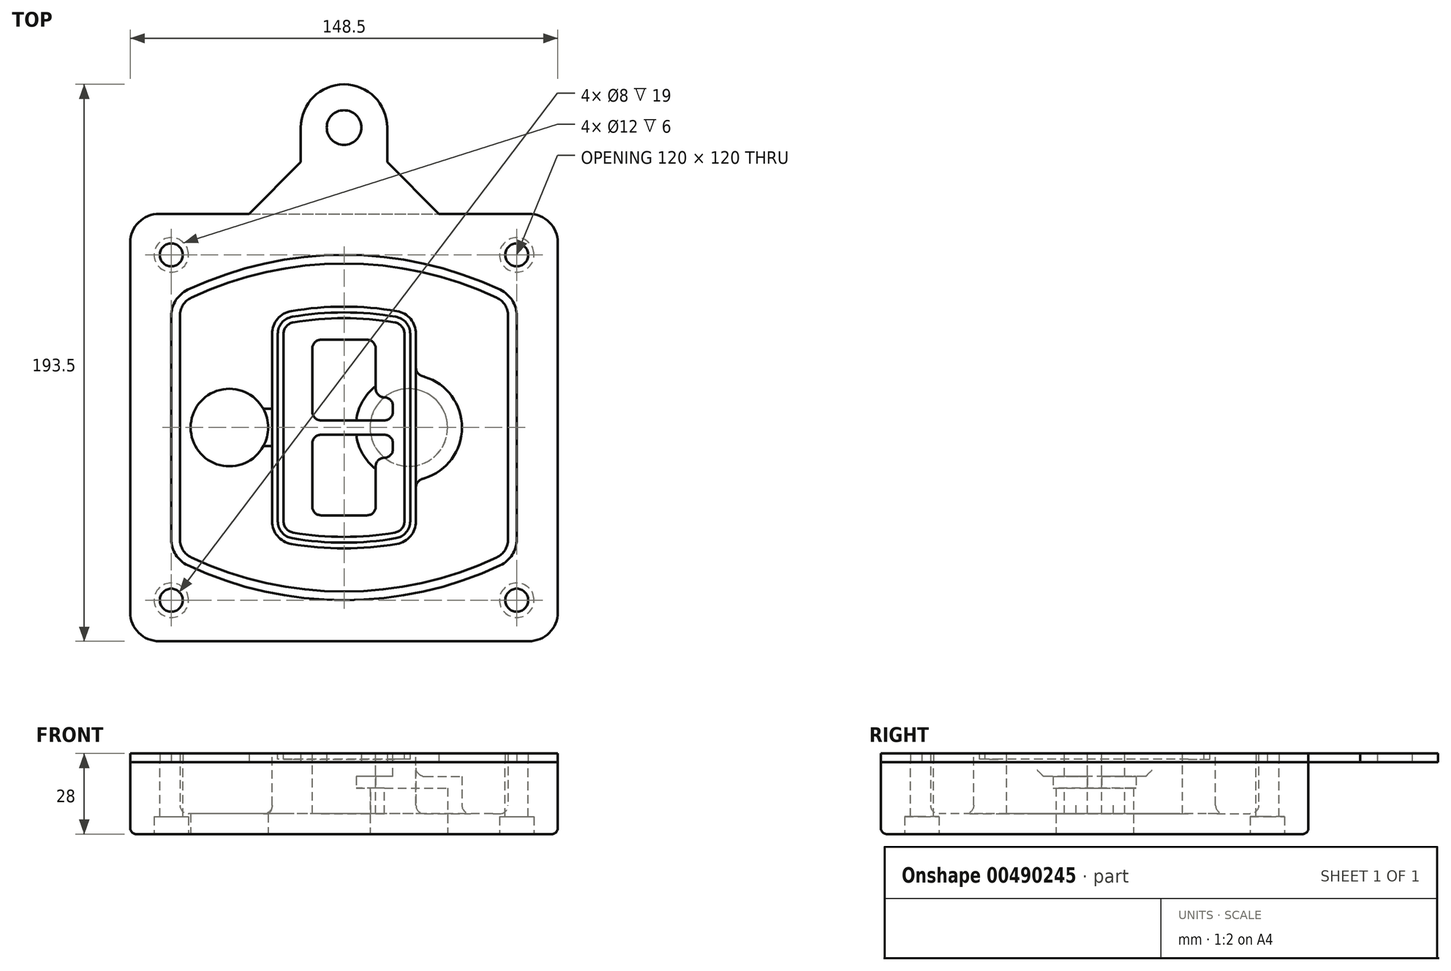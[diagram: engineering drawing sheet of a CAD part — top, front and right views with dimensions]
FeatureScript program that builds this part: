
annotation { "Feature Type Name" : "Feature", "Feature Type Description" : "" }
export const myFeature = defineFeature(function(context is Context, id is Id, definition is map)
    precondition{}
    {
        {
            var Q0;
            Q0=qCreatedBy(makeId("Top.planeOp"),FACE);
            var sketch = newSketch(context, id + "F0", { "sketchPlane" : qUnion([Q0])});
            skPoint(sketch, "E0.rect.middle", {"position": v(0, 0) * mm});
            skLineSegment(sketch, "E1.bottom", {"start": v(-64.25, -74.25) * mm, "end": v(64.25, -74.25) * mm});
            skLineSegment(sketch, "E1.top", {"start": v(-64.25, 74.25) * mm, "end": v(64.25, 74.25) * mm});
            skLineSegment(sketch, "E1.left", {"start": v(-74.25, -64.25) * mm, "end": v(-74.25, 64.25) * mm});
            skLineSegment(sketch, "E1.right", {"start": v(74.25, -64.25) * mm, "end": v(74.25, 64.25) * mm});
            skLineSegment(sketch, "E2", {"start": v(-74.25, 74.25) * mm, "end": v(74.25, -74.25) * mm, "construction": true});
            skLineSegment(sketch, "E3", {"start": v(74.25, 74.25) * mm, "end": v(-74.25, -74.25) * mm, "construction": true});
            skCircle(sketch, "E4", {"center": v(-60, 60) * mm, "radius": 4 * mm});
            skCircle(sketch, "E5", {"center": v(60, 60) * mm, "radius": 4 * mm});
            skCircle(sketch, "E6", {"center": v(60, -60) * mm, "radius": 4 * mm});
            skCircle(sketch, "E7", {"center": v(-60, -60) * mm, "radius": 4 * mm});
            skLineSegment(sketch, "E8", {"start": v(-60, 60) * mm, "end": v(60, 60) * mm, "construction": true});
            skLineSegment(sketch, "E9", {"start": v(60, 60) * mm, "end": v(60, -60) * mm, "construction": true});
            skLineSegment(sketch, "E10", {"start": v(60, -60) * mm, "end": v(-60, -60) * mm, "construction": true});
            skLineSegment(sketch, "E11", {"start": v(-60, -60) * mm, "end": v(-60, 60) * mm, "construction": true});
            skLineSegment(sketch, "E12", {"start": v(-60, 38.83) * mm, "end": v(-60, -38.83) * mm});
            skLineSegment(sketch, "E13", {"start": v(60, 38.83) * mm, "end": v(60, -38.83) * mm});
            skArc(sketch, "E14", {"start": v(54.26, 47.88) * mm, "mid": v(0, 60) * mm, "end": v(-54.26, 47.88) * mm});
            skArc(sketch, "E15", {"start": v(-54.26, -47.88) * mm, "mid": v(0, -60) * mm, "end": v(54.26, -47.88) * mm});
            skLineSegment(sketch, "E16", {"start": v(-60, 0) * mm, "end": v(60, 0) * mm, "construction": true});
            skPoint(sketch, "E17.visualSharp", {"position": v(-60, -45) * mm});
            skArc(sketch, "E17.filletArc", {"start": v(-60, -38.83) * mm, "mid": v(-58.44, -44.2) * mm, "end": v(-54.26, -47.88) * mm});
            skPoint(sketch, "E18.visualSharp", {"position": v(-60, 45) * mm});
            skArc(sketch, "E18.filletArc", {"start": v(-54.26, 47.88) * mm, "mid": v(-58.44, 44.2) * mm, "end": v(-60, 38.83) * mm});
            skPoint(sketch, "E19.visualSharp", {"position": v(60, 45) * mm});
            skArc(sketch, "E19.filletArc", {"start": v(60, 38.83) * mm, "mid": v(58.44, 44.2) * mm, "end": v(54.26, 47.88) * mm});
            skPoint(sketch, "E20.visualSharp", {"position": v(60, -45) * mm});
            skArc(sketch, "E20.filletArc", {"start": v(54.26, -47.88) * mm, "mid": v(58.44, -44.2) * mm, "end": v(60, -38.83) * mm});
            skPoint(sketch, "E21.visualSharp", {"position": v(-74.25, 74.25) * mm});
            skArc(sketch, "E21.filletArc", {"start": v(-64.25, 74.25) * mm, "mid": v(-71.32, 71.32) * mm, "end": v(-74.25, 64.25) * mm});
            skPoint(sketch, "E22.visualSharp", {"position": v(74.25, 74.25) * mm});
            skArc(sketch, "E22.filletArc", {"start": v(74.25, 64.25) * mm, "mid": v(71.32, 71.32) * mm, "end": v(64.25, 74.25) * mm});
            skPoint(sketch, "E23.visualSharp", {"position": v(74.25, -74.25) * mm});
            skArc(sketch, "E23.filletArc", {"start": v(64.25, -74.25) * mm, "mid": v(71.32, -71.32) * mm, "end": v(74.25, -64.25) * mm});
            skPoint(sketch, "E24.visualSharp", {"position": v(-74.25, -74.25) * mm});
            skArc(sketch, "E24.filletArc", {"start": v(-74.25, -64.25) * mm, "mid": v(-71.32, -71.32) * mm, "end": v(-64.25, -74.25) * mm});
            skArc(sketch, "E25.0", {"start": v(57, 38.83) * mm, "mid": v(55.9, 42.58) * mm, "end": v(52.98, 45.17) * mm});
            skLineSegment(sketch, "E25.1", {"start": v(57, 38.83) * mm, "end": v(57, -38.83) * mm});
            skArc(sketch, "E25.2", {"start": v(52.98, -45.17) * mm, "mid": v(55.9, -42.58) * mm, "end": v(57, -38.83) * mm});
            skArc(sketch, "E25.3", {"start": v(-52.98, -45.17) * mm, "mid": v(0, -57) * mm, "end": v(52.98, -45.17) * mm});
            skArc(sketch, "E25.4", {"start": v(-57, -38.83) * mm, "mid": v(-55.9, -42.58) * mm, "end": v(-52.98, -45.17) * mm});
            skArc(sketch, "E25.5", {"start": v(52.98, 45.17) * mm, "mid": v(0, 57) * mm, "end": v(-52.98, 45.17) * mm});
            skLineSegment(sketch, "E25.6", {"start": v(-57, 38.83) * mm, "end": v(-57, -38.83) * mm});
            skArc(sketch, "E25.7", {"start": v(-52.98, 45.17) * mm, "mid": v(-55.9, 42.58) * mm, "end": v(-57, 38.83) * mm});
            skArc(sketch, "E26.0", {"start": v(-55.96, 51.5) * mm, "mid": v(-61.82, 46.33) * mm, "end": v(-64, 38.83) * mm});
            skArc(sketch, "E26.1", {"start": v(55.96, 51.5) * mm, "mid": v(0, 64) * mm, "end": v(-55.96, 51.5) * mm});
            skArc(sketch, "E26.2", {"start": v(64, 38.83) * mm, "mid": v(61.82, 46.33) * mm, "end": v(55.96, 51.5) * mm});
            skLineSegment(sketch, "E26.3", {"start": v(64, 38.83) * mm, "end": v(64, -38.83) * mm});
            skArc(sketch, "E26.4", {"start": v(55.96, -51.5) * mm, "mid": v(61.82, -46.33) * mm, "end": v(64, -38.83) * mm});
            skLineSegment(sketch, "E26.5", {"start": v(-64, 38.83) * mm, "end": v(-64, -38.83) * mm});
            skArc(sketch, "E26.6", {"start": v(-55.96, -51.5) * mm, "mid": v(0, -64) * mm, "end": v(55.96, -51.5) * mm});
            skArc(sketch, "E26.7", {"start": v(-64, -38.83) * mm, "mid": v(-61.82, -46.33) * mm, "end": v(-55.96, -51.5) * mm});
            skSolve(sketch);
        }
        {
            var Q0;
            Q0=makeQuery(id+"F0.imprint","IMPRINT",FACE,{"disambiguationData":[TD([[makeQuery(id+"F0.imprint","IMPRINT",EDGE,{"derivedFrom":sQuery(id+"F0.wireOp",EDGE,"E1.bottom")}),1.0]])]});
            var Q1;
            Q1=makeQuery(id+"F0.imprint","IMPRINT",FACE,{"disambiguationData":[TD([[makeQuery(id+"F0.imprint","IMPRINT",EDGE,{"derivedFrom":sQuery(id+"F0.wireOp",EDGE,"E12")}),1.0]])]});
            var Q2;
            Q2=makeQuery(id+"F0.imprint","IMPRINT",FACE,{"disambiguationData":[TD([[makeQuery(id+"F0.imprint","IMPRINT",EDGE,{"derivedFrom":sQuery(id+"F0.wireOp",EDGE,"E25.0")}),1.0]])]});
            var Q3;
            Q3=makeQuery(id+"F0.imprint","IMPRINT",FACE,{"disambiguationData":[TD([[makeQuery(id+"F0.imprint","IMPRINT",EDGE,{"derivedFrom":sQuery(id+"F0.wireOp",EDGE,"E12")}),-1.0]])]});
            extrude(context, id + "F1", {"entities" : qUnion([Q0, Q1, Q2, Q3]), "oppositeDirection" : true, "depth" : 25 * mm});
        }
        {
            var Q0;
            Q0=makeQuery(id+"F0.imprint","IMPRINT",FACE,{"disambiguationData":[TD([[makeQuery(id+"F0.imprint","IMPRINT",EDGE,{"derivedFrom":sQuery(id+"F0.wireOp",EDGE,"E12")}),1.0]])]});
            extrude(context, id + "F2", {"entities" : qUnion([Q0]), "operationType" : NewBodyOperationType.ADD, "depth" : 3 * mm});
        }
        {
            var Q0;
            Q0=makeQuery(id+"F0.imprint","IMPRINT",FACE,{"disambiguationData":[TD([[makeQuery(id+"F0.imprint","IMPRINT",EDGE,{"derivedFrom":sQuery(id+"F0.wireOp",EDGE,"E25.0")}),1.0]])]});
            extrude(context, id + "F3", {"entities" : qUnion([Q0]), "operationType" : NewBodyOperationType.REMOVE, "oppositeDirection" : true, "depth" : 18 * mm});
        }
        {
            var Q0;
            Q0=makeQuery(id+"F2.opExtrude","CAP_FACE",FACE,{"disambiguationData":[OSD([sQuery(id+"F0.wireOp",EDGE,"E12"),sQuery(id+"F0.wireOp",EDGE,"E13"),sQuery(id+"F0.wireOp",EDGE,"E14"),sQuery(id+"F0.wireOp",EDGE,"E15"),sQuery(id+"F0.wireOp",EDGE,"E17.filletArc"),sQuery(id+"F0.wireOp",EDGE,"E18.filletArc"),sQuery(id+"F0.wireOp",EDGE,"E19.filletArc"),sQuery(id+"F0.wireOp",EDGE,"E20.filletArc"),sQuery(id+"F0.wireOp",EDGE,"E25.0"),sQuery(id+"F0.wireOp",EDGE,"E25.1"),sQuery(id+"F0.wireOp",EDGE,"E25.2"),sQuery(id+"F0.wireOp",EDGE,"E25.3"),sQuery(id+"F0.wireOp",EDGE,"E25.4"),sQuery(id+"F0.wireOp",EDGE,"E25.5"),sQuery(id+"F0.wireOp",EDGE,"E25.6"),sQuery(id+"F0.wireOp",EDGE,"E25.7")])],"isStart":false});
            var sketch = newSketch(context, id + "F4", { "sketchPlane" : qUnion([Q0])});
            skArc(sketch, "E27.0", {"start": v(-18.34, -40.45) * mm, "mid": v(0, -42) * mm, "end": v(18.34, -40.45) * mm});
            skArc(sketch, "E28.0", {"start": v(18.34, 40.45) * mm, "mid": v(0, 42) * mm, "end": v(-18.34, 40.45) * mm});
            skLineSegment(sketch, "E29", {"start": v(-25, 32.57) * mm, "end": v(-25, -32.57) * mm});
            skLineSegment(sketch, "E30", {"start": v(25, 32.57) * mm, "end": v(25, -32.57) * mm});
            skLineSegment(sketch, "E31", {"start": v(-25, 39.1) * mm, "end": v(25, 39.1) * mm, "construction": true});
            skLineSegment(sketch, "E32", {"start": v(-25, -39.1) * mm, "end": v(25, -39.1) * mm, "construction": true});
            skPoint(sketch, "E33.visualSharp", {"position": v(-25, 39.1) * mm});
            skArc(sketch, "E33.filletArc", {"start": v(-18.34, 40.45) * mm, "mid": v(-23.11, 37.73) * mm, "end": v(-25, 32.57) * mm});
            skPoint(sketch, "E34.visualSharp", {"position": v(25, 39.1) * mm});
            skArc(sketch, "E34.filletArc", {"start": v(25, 32.57) * mm, "mid": v(23.11, 37.73) * mm, "end": v(18.34, 40.45) * mm});
            skPoint(sketch, "E35.visualSharp", {"position": v(25, -39.1) * mm});
            skArc(sketch, "E35.filletArc", {"start": v(18.34, -40.45) * mm, "mid": v(23.11, -37.73) * mm, "end": v(25, -32.57) * mm});
            skPoint(sketch, "E36.visualSharp", {"position": v(-25, -39.1) * mm});
            skArc(sketch, "E36.filletArc", {"start": v(-25, -32.57) * mm, "mid": v(-23.11, -37.73) * mm, "end": v(-18.34, -40.45) * mm});
            skArc(sketch, "E37.0", {"start": v(52.98, 45.17) * mm, "mid": v(0, 57) * mm, "end": v(-52.98, 45.17) * mm});
            skArc(sketch, "E37.1", {"start": v(-52.98, 45.17) * mm, "mid": v(-55.9, 42.58) * mm, "end": v(-57, 38.83) * mm});
            skLineSegment(sketch, "E37.2", {"start": v(-57, 38.83) * mm, "end": v(-57, -38.83) * mm});
            skArc(sketch, "E37.3", {"start": v(-57, -38.83) * mm, "mid": v(-55.9, -42.58) * mm, "end": v(-52.98, -45.17) * mm});
            skArc(sketch, "E37.4", {"start": v(-52.98, -45.17) * mm, "mid": v(0, -57) * mm, "end": v(52.98, -45.17) * mm});
            skArc(sketch, "E37.5", {"start": v(52.98, -45.17) * mm, "mid": v(55.9, -42.58) * mm, "end": v(57, -38.83) * mm});
            skLineSegment(sketch, "E37.6", {"start": v(57, 38.83) * mm, "end": v(57, -38.83) * mm});
            skArc(sketch, "E37.7", {"start": v(57, 38.83) * mm, "mid": v(55.9, 42.58) * mm, "end": v(52.98, 45.17) * mm});
            skLineSegment(sketch, "E38.0", {"start": v(23, 32.57) * mm, "end": v(23, -32.57) * mm});
            skArc(sketch, "E38.1", {"start": v(18, -38.48) * mm, "mid": v(21.58, -36.44) * mm, "end": v(23, -32.57) * mm});
            skArc(sketch, "E38.2", {"start": v(-18, -38.48) * mm, "mid": v(0, -40) * mm, "end": v(18, -38.48) * mm});
            skArc(sketch, "E38.3", {"start": v(-23, -32.57) * mm, "mid": v(-21.58, -36.44) * mm, "end": v(-18, -38.48) * mm});
            skLineSegment(sketch, "E38.4", {"start": v(-23, 32.57) * mm, "end": v(-23, -32.57) * mm});
            skArc(sketch, "E38.5", {"start": v(23, 32.57) * mm, "mid": v(21.58, 36.44) * mm, "end": v(18, 38.48) * mm});
            skArc(sketch, "E38.6", {"start": v(-18, 38.48) * mm, "mid": v(-21.58, 36.44) * mm, "end": v(-23, 32.57) * mm});
            skArc(sketch, "E38.7", {"start": v(18, 38.48) * mm, "mid": v(0, 40) * mm, "end": v(-18, 38.48) * mm});
            skArc(sketch, "E39.0", {"start": v(21, 32.57) * mm, "mid": v(20.06, 35.15) * mm, "end": v(17.67, 36.5) * mm});
            skLineSegment(sketch, "E39.1", {"start": v(21, 32.57) * mm, "end": v(21, -32.57) * mm});
            skArc(sketch, "E39.2", {"start": v(17.67, -36.5) * mm, "mid": v(20.06, -35.15) * mm, "end": v(21, -32.57) * mm});
            skArc(sketch, "E39.3", {"start": v(-17.67, -36.5) * mm, "mid": v(0, -38) * mm, "end": v(17.67, -36.5) * mm});
            skArc(sketch, "E39.4", {"start": v(-21, -32.57) * mm, "mid": v(-20.06, -35.15) * mm, "end": v(-17.67, -36.5) * mm});
            skArc(sketch, "E39.5", {"start": v(17.67, 36.5) * mm, "mid": v(0, 38) * mm, "end": v(-17.67, 36.5) * mm});
            skLineSegment(sketch, "E39.6", {"start": v(-21, 32.57) * mm, "end": v(-21, -32.57) * mm});
            skArc(sketch, "E39.7", {"start": v(-17.67, 36.5) * mm, "mid": v(-20.06, 35.15) * mm, "end": v(-21, 32.57) * mm});
            skLineSegment(sketch, "E40", {"start": v(-25, 0) * mm, "end": v(25, 0) * mm, "construction": true});
            skLineSegment(sketch, "E41", {"start": v(-11, 5.5) * mm, "end": v(-11, 27.5) * mm});
            skLineSegment(sketch, "E42", {"start": v(-8, 30.5) * mm, "end": v(8, 30.5) * mm});
            skLineSegment(sketch, "E43", {"start": v(11, 27.5) * mm, "end": v(11, 13.5) * mm});
            skLineSegment(sketch, "E44", {"start": v(14, 10.5) * mm, "end": v(14, 10.5) * mm});
            skLineSegment(sketch, "E45", {"start": v(17, 7.5) * mm, "end": v(17, 5.5) * mm});
            skLineSegment(sketch, "E46", {"start": v(14, 2.5) * mm, "end": v(-8, 2.5) * mm});
            skPoint(sketch, "E47.visualSharp", {"position": v(-11, 30.5) * mm});
            skArc(sketch, "E47.filletArc", {"start": v(-8, 30.5) * mm, "mid": v(-10.12, 29.62) * mm, "end": v(-11, 27.5) * mm});
            skPoint(sketch, "E48.visualSharp", {"position": v(11, 30.5) * mm});
            skArc(sketch, "E48.filletArc", {"start": v(11, 27.5) * mm, "mid": v(10.12, 29.62) * mm, "end": v(8, 30.5) * mm});
            skPoint(sketch, "E49.visualSharp", {"position": v(11, 10.5) * mm});
            skArc(sketch, "E49.filletArc", {"start": v(11, 13.5) * mm, "mid": v(11.88, 11.38) * mm, "end": v(14, 10.5) * mm});
            skPoint(sketch, "E50.visualSharp", {"position": v(17, 10.5) * mm});
            skArc(sketch, "E50.filletArc", {"start": v(17, 7.5) * mm, "mid": v(16.12, 9.62) * mm, "end": v(14, 10.5) * mm});
            skPoint(sketch, "E51.visualSharp", {"position": v(17, 2.5) * mm});
            skArc(sketch, "E51.filletArc", {"start": v(14, 2.5) * mm, "mid": v(16.12, 3.38) * mm, "end": v(17, 5.5) * mm});
            skPoint(sketch, "E52.visualSharp", {"position": v(-11, 2.5) * mm});
            skArc(sketch, "E52.filletArc", {"start": v(-11, 5.5) * mm, "mid": v(-10.12, 3.38) * mm, "end": v(-8, 2.5) * mm});
            skLineSegment(sketch, "E53.0.MirrorCS", {"start": v(14, -2.5) * mm, "end": v(-8, -2.5) * mm});
            skArc(sketch, "E54.0.MirrorCS", {"start": v(-11, -5.5) * mm, "mid": v(-10.12, -3.38) * mm, "end": v(-8, -2.5) * mm});
            skLineSegment(sketch, "E55.0.MirrorCS", {"start": v(-11, -5.5) * mm, "end": v(-11, -27.5) * mm});
            skArc(sketch, "E56.0.MirrorCS", {"start": v(-8, -30.5) * mm, "mid": v(-10.12, -29.62) * mm, "end": v(-11, -27.5) * mm});
            skLineSegment(sketch, "E57.0.MirrorCS", {"start": v(-8, -30.5) * mm, "end": v(8, -30.5) * mm});
            skArc(sketch, "E58.0.MirrorCS", {"start": v(11, -27.5) * mm, "mid": v(10.12, -29.62) * mm, "end": v(8, -30.5) * mm});
            skLineSegment(sketch, "E59.0.MirrorCS", {"start": v(11, -27.5) * mm, "end": v(11, -13.5) * mm});
            skArc(sketch, "E60.0.MirrorCS", {"start": v(11, -13.5) * mm, "mid": v(11.88, -11.38) * mm, "end": v(14, -10.5) * mm});
            skArc(sketch, "E61.0.MirrorCS", {"start": v(17, -7.5) * mm, "mid": v(16.12, -9.62) * mm, "end": v(14, -10.5) * mm});
            skLineSegment(sketch, "E62.0.MirrorCS", {"start": v(17, -7.5) * mm, "end": v(17, -5.5) * mm});
            skArc(sketch, "E63.0.MirrorCS", {"start": v(14, -2.5) * mm, "mid": v(16.12, -3.38) * mm, "end": v(17, -5.5) * mm});
            skSolve(sketch);
        }
        {
            var Q0;
            Q0=makeQuery(id+"F4.imprint","IMPRINT",FACE,{"disambiguationData":[TD([[makeQuery(id+"F4.imprint","IMPRINT",EDGE,{"derivedFrom":sQuery(id+"F4.wireOp",EDGE,"E27.0")}),1.0]])]});
            var Q1;
            Q1=makeQuery(id+"F4.imprint","IMPRINT",FACE,{"disambiguationData":[TD([[makeQuery(id+"F4.imprint","IMPRINT",EDGE,{"derivedFrom":sQuery(id+"F4.wireOp",EDGE,"E38.0")}),-1.0]])]});
            var Q2;
            Q2=makeQuery(id+"F4.imprint","IMPRINT",FACE,{"disambiguationData":[TD([[makeQuery(id+"F4.imprint","IMPRINT",EDGE,{"derivedFrom":sQuery(id+"F4.wireOp",EDGE,"E39.0")}),1.0]])]});
            extrude(context, id + "F5", {"entities" : qUnion([Q0, Q1, Q2]), "operationType" : NewBodyOperationType.ADD, "endBound" : BoundingType.UP_TO_NEXT, "oppositeDirection" : true, "depth" : 25 * mm});
        }
        {
            var Q0;
            Q0=makeQuery(id+"F4.imprint","IMPRINT",FACE,{"disambiguationData":[TD([[makeQuery(id+"F4.imprint","IMPRINT",EDGE,{"derivedFrom":sQuery(id+"F4.wireOp",EDGE,"E38.0")}),-1.0]])]});
            extrude(context, id + "F6", {"entities" : qUnion([Q0]), "operationType" : NewBodyOperationType.REMOVE, "oppositeDirection" : true, "depth" : 2 * mm});
        }
        {
            var Q0;
            Q0=makeQuery(id+"F1.opExtrude","CAP_FACE",FACE,{"disambiguationData":[OSD([sQuery(id+"F0.wireOp",EDGE,"E1.bottom"),sQuery(id+"F0.wireOp",EDGE,"E1.top"),sQuery(id+"F0.wireOp",EDGE,"E1.left"),sQuery(id+"F0.wireOp",EDGE,"E1.right"),sQuery(id+"F0.wireOp",EDGE,"E4"),sQuery(id+"F0.wireOp",EDGE,"E5"),sQuery(id+"F0.wireOp",EDGE,"E6"),sQuery(id+"F0.wireOp",EDGE,"E7"),sQuery(id+"F0.wireOp",EDGE,"E21.filletArc"),sQuery(id+"F0.wireOp",EDGE,"E22.filletArc"),sQuery(id+"F0.wireOp",EDGE,"E23.filletArc"),sQuery(id+"F0.wireOp",EDGE,"E24.filletArc")])],"isStart":false});
            var sketch = newSketch(context, id + "F7", { "sketchPlane" : qUnion([Q0])});
            skCircle(sketch, "E64", {"center": v(22.5, 0) * mm, "radius": 13.47 * mm});
            skCircle(sketch, "E65", {"center": v(-39.81, 0) * mm, "radius": 13.47 * mm});
            skLineSegment(sketch, "E66", {"start": v(74.25, 0) * mm, "end": v(-74.25, 0) * mm});
            skCircle(sketch, "E67", {"center": v(22.5, 0) * mm, "radius": 18.47 * mm});
            skCircle(sketch, "E68", {"center": v(60, -60) * mm, "radius": 6 * mm});
            skCircle(sketch, "E69", {"center": v(-60, -60) * mm, "radius": 6 * mm});
            skCircle(sketch, "E70", {"center": v(-60, 60) * mm, "radius": 6 * mm});
            skCircle(sketch, "E71", {"center": v(60, 60) * mm, "radius": 6 * mm});
            skSolve(sketch);
        }
        {
            var Q0;
            {var subQ1=sQuery(id+"F7.wireOp",EDGE,"E66");var subQ4=sQuery(id+"F7.wireOp",EDGE,"E64");var subQ6=makeQuery(id+"F7.imprint","INTERSECT",VERTEX,{"disambiguationData":[OD(0.0)],"derivedFrom":[subQ4,subQ1]});Q0=makeQuery(id+"F7.imprint","IMPRINT",FACE,{"disambiguationData":[TD([[makeQuery(id+"F7.imprint","IMPRINT",EDGE,{"disambiguationData":[TD([[subQ6,-1.0]])],"derivedFrom":subQ4}),-1.0]])]});}
            var Q1;
            {var subQ0=sQuery(id+"F7.wireOp",EDGE,"E66");var subQ1=sQuery(id+"F7.wireOp",EDGE,"E64");var subQ3=makeQuery(id+"F7.imprint","INTERSECT",VERTEX,{"disambiguationData":[OD(0.0)],"derivedFrom":[subQ1,subQ0]});Q1=makeQuery(id+"F7.imprint","IMPRINT",FACE,{"disambiguationData":[TD([[makeQuery(id+"F7.imprint","IMPRINT",EDGE,{"disambiguationData":[TD([[subQ3,-1.0]])],"derivedFrom":subQ1}),1.0]])]});}
            var Q2;
            {var subQ0=sQuery(id+"F7.wireOp",EDGE,"E66");var subQ1=sQuery(id+"F7.wireOp",EDGE,"E64");var subQ3=makeQuery(id+"F7.imprint","INTERSECT",VERTEX,{"disambiguationData":[OD(0.0)],"derivedFrom":[subQ1,subQ0]});Q2=makeQuery(id+"F7.imprint","IMPRINT",FACE,{"disambiguationData":[TD([[makeQuery(id+"F7.imprint","IMPRINT",EDGE,{"disambiguationData":[TD([[subQ3,1.0]])],"derivedFrom":subQ1}),1.0]])]});}
            var Q3;
            {var subQ1=sQuery(id+"F7.wireOp",EDGE,"E66");var subQ4=sQuery(id+"F7.wireOp",EDGE,"E64");var subQ6=makeQuery(id+"F7.imprint","INTERSECT",VERTEX,{"disambiguationData":[OD(0.0)],"derivedFrom":[subQ4,subQ1]});Q3=makeQuery(id+"F7.imprint","IMPRINT",FACE,{"disambiguationData":[TD([[makeQuery(id+"F7.imprint","IMPRINT",EDGE,{"disambiguationData":[TD([[subQ6,1.0]])],"derivedFrom":subQ4}),-1.0]])]});}
            extrude(context, id + "F8", {"entities" : qUnion([Q0, Q1, Q2, Q3]), "operationType" : NewBodyOperationType.ADD, "oppositeDirection" : true, "depth" : 20 * mm});
        }
        {
            var Q0;
            {var subQ0=sQuery(id+"F7.wireOp",EDGE,"E66");var subQ1=sQuery(id+"F7.wireOp",EDGE,"E64");var subQ3=makeQuery(id+"F7.imprint","INTERSECT",VERTEX,{"disambiguationData":[OD(0.0)],"derivedFrom":[subQ1,subQ0]});Q0=makeQuery(id+"F7.imprint","IMPRINT",FACE,{"disambiguationData":[TD([[makeQuery(id+"F7.imprint","IMPRINT",EDGE,{"disambiguationData":[TD([[subQ3,-1.0]])],"derivedFrom":subQ1}),1.0]])]});}
            var Q1;
            {var subQ0=sQuery(id+"F7.wireOp",EDGE,"E66");var subQ1=sQuery(id+"F7.wireOp",EDGE,"E64");var subQ3=makeQuery(id+"F7.imprint","INTERSECT",VERTEX,{"disambiguationData":[OD(0.0)],"derivedFrom":[subQ1,subQ0]});Q1=makeQuery(id+"F7.imprint","IMPRINT",FACE,{"disambiguationData":[TD([[makeQuery(id+"F7.imprint","IMPRINT",EDGE,{"disambiguationData":[TD([[subQ3,1.0]])],"derivedFrom":subQ1}),1.0]])]});}
            extrude(context, id + "F9", {"entities" : qUnion([Q0, Q1]), "operationType" : NewBodyOperationType.REMOVE, "oppositeDirection" : true, "depth" : 16 * mm});
        }
        {
            var Q0;
            {var subQ0=sQuery(id+"F7.wireOp",EDGE,"E66");var subQ1=sQuery(id+"F7.wireOp",EDGE,"E65");var subQ3=makeQuery(id+"F7.imprint","INTERSECT",VERTEX,{"disambiguationData":[OD(0.0)],"derivedFrom":[subQ1,subQ0]});Q0=makeQuery(id+"F7.imprint","IMPRINT",FACE,{"disambiguationData":[TD([[makeQuery(id+"F7.imprint","IMPRINT",EDGE,{"disambiguationData":[TD([[subQ3,-1.0]])],"derivedFrom":subQ1}),1.0]])]});}
            var Q1;
            {var subQ0=sQuery(id+"F7.wireOp",EDGE,"E66");var subQ1=sQuery(id+"F7.wireOp",EDGE,"E65");var subQ3=makeQuery(id+"F7.imprint","INTERSECT",VERTEX,{"disambiguationData":[OD(0.0)],"derivedFrom":[subQ1,subQ0]});Q1=makeQuery(id+"F7.imprint","IMPRINT",FACE,{"disambiguationData":[TD([[makeQuery(id+"F7.imprint","IMPRINT",EDGE,{"disambiguationData":[TD([[subQ3,1.0]])],"derivedFrom":subQ1}),1.0]])]});}
            extrude(context, id + "F10", {"entities" : qUnion([Q0, Q1]), "operationType" : NewBodyOperationType.REMOVE, "oppositeDirection" : true, "depth" : 25 * mm});
        }
        {
            var Q0;
            Q0=makeQuery(id+"F7.imprint","IMPRINT",FACE,{"disambiguationData":[TD([[makeQuery(id+"F7.imprint","IMPRINT",EDGE,{"derivedFrom":sQuery(id+"F7.wireOp",EDGE,"E68")}),1.0]])]});
            var Q1;
            Q1=makeQuery(id+"F7.imprint","IMPRINT",FACE,{"disambiguationData":[TD([[makeQuery(id+"F7.imprint","IMPRINT",EDGE,{"derivedFrom":makeQuery(id+"F1.opExtrude","CAP_EDGE",EDGE,{"disambiguationData":[OSD([sQuery(id+"F0.wireOp",EDGE,"E5")])],"isStart":false})}),-1.0]])]});
            var Q2;
            Q2=makeQuery(id+"F7.imprint","IMPRINT",FACE,{"disambiguationData":[TD([[makeQuery(id+"F7.imprint","IMPRINT",EDGE,{"derivedFrom":sQuery(id+"F7.wireOp",EDGE,"E69")}),1.0]])]});
            var Q3;
            Q3=makeQuery(id+"F7.imprint","IMPRINT",FACE,{"disambiguationData":[TD([[makeQuery(id+"F7.imprint","IMPRINT",EDGE,{"derivedFrom":makeQuery(id+"F1.opExtrude","CAP_EDGE",EDGE,{"disambiguationData":[OSD([sQuery(id+"F0.wireOp",EDGE,"E4")])],"isStart":false})}),-1.0]])]});
            var Q4;
            Q4=makeQuery(id+"F7.imprint","IMPRINT",FACE,{"disambiguationData":[TD([[makeQuery(id+"F7.imprint","IMPRINT",EDGE,{"derivedFrom":sQuery(id+"F7.wireOp",EDGE,"E70")}),1.0]])]});
            var Q5;
            Q5=makeQuery(id+"F7.imprint","IMPRINT",FACE,{"disambiguationData":[TD([[makeQuery(id+"F7.imprint","IMPRINT",EDGE,{"derivedFrom":makeQuery(id+"F1.opExtrude","CAP_EDGE",EDGE,{"disambiguationData":[OSD([sQuery(id+"F0.wireOp",EDGE,"E7")])],"isStart":false})}),-1.0]])]});
            var Q6;
            Q6=makeQuery(id+"F7.imprint","IMPRINT",FACE,{"disambiguationData":[TD([[makeQuery(id+"F7.imprint","IMPRINT",EDGE,{"derivedFrom":sQuery(id+"F7.wireOp",EDGE,"E71")}),1.0]])]});
            var Q7;
            Q7=makeQuery(id+"F7.imprint","IMPRINT",FACE,{"disambiguationData":[TD([[makeQuery(id+"F7.imprint","IMPRINT",EDGE,{"derivedFrom":makeQuery(id+"F1.opExtrude","CAP_EDGE",EDGE,{"disambiguationData":[OSD([sQuery(id+"F0.wireOp",EDGE,"E6")])],"isStart":false})}),-1.0]])]});
            extrude(context, id + "F11", {"entities" : qUnion([Q0, Q1, Q2, Q3, Q4, Q5, Q6, Q7]), "operationType" : NewBodyOperationType.REMOVE, "oppositeDirection" : true, "depth" : 6 * mm});
        }
        {
            var Q0;
            Q0=makeQuery(id+"F9.boolean.opBoolean","COPY",FACE,{"derivedFrom":makeQuery(id+"F9.opExtrude","CAP_FACE",FACE,{"disambiguationData":[OSD([sQuery(id+"F7.wireOp",EDGE,"E64")])],"isStart":false})});
            var sketch = newSketch(context, id + "F12", { "sketchPlane" : qUnion([Q0])});
            skArc(sketch, "E72.0", {"start": v(11, 14.45) * mm, "mid": v(6.45, 9.13) * mm, "end": v(4.2, 2.5) * mm});
            skArc(sketch, "E72.1", {"start": v(4.2, -2.5) * mm, "mid": v(6.45, -9.13) * mm, "end": v(11, -14.45) * mm});
            skLineSegment(sketch, "E73", {"start": v(4.2, -2.5) * mm, "end": v(14, -2.5) * mm});
            skLineSegment(sketch, "E74.0", {"start": v(14, 2.5) * mm, "end": v(4.2, 2.5) * mm});
            skArc(sketch, "E74.1", {"start": v(14, 2.5) * mm, "mid": v(16.12, 3.38) * mm, "end": v(17, 5.5) * mm});
            skLineSegment(sketch, "E74.2", {"start": v(17, 7.5) * mm, "end": v(17, 5.5) * mm});
            skArc(sketch, "E74.3", {"start": v(17, 7.5) * mm, "mid": v(16.12, 9.62) * mm, "end": v(14, 10.5) * mm});
            skArc(sketch, "E74.4", {"start": v(11, 13.5) * mm, "mid": v(11.88, 11.38) * mm, "end": v(14, 10.5) * mm});
            skLineSegment(sketch, "E74.5", {"start": v(11, 14.45) * mm, "end": v(11, 13.5) * mm});
            skLineSegment(sketch, "E74.7", {"start": v(14, -2.5) * mm, "end": v(4.2, -2.5) * mm});
            skArc(sketch, "E74.8", {"start": v(14, -2.5) * mm, "mid": v(16.12, -3.38) * mm, "end": v(17, -5.5) * mm});
            skLineSegment(sketch, "E74.9", {"start": v(17, -7.5) * mm, "end": v(17, -5.5) * mm});
            skArc(sketch, "E74.10", {"start": v(17, -7.5) * mm, "mid": v(16.12, -9.62) * mm, "end": v(14, -10.5) * mm});
            skArc(sketch, "E74.11", {"start": v(11, -13.5) * mm, "mid": v(11.88, -11.38) * mm, "end": v(14, -10.5) * mm});
            skLineSegment(sketch, "E74.12", {"start": v(11, -14.45) * mm, "end": v(11, -13.5) * mm});
            skPoint(sketch, "E75.orphan", {"position": v(11, -27.5) * mm});
            skPoint(sketch, "E76.orphan", {"position": v(-8, -2.5) * mm});
            skPoint(sketch, "E77.orphan", {"position": v(-8, 2.5) * mm});
            skPoint(sketch, "E78.orphan", {"position": v(11, 27.5) * mm});
            skSolve(sketch);
        }
        {
            var Q0;
            {var subQ7=sQuery(id+"F12.wireOp",EDGE,"E72.0");var subQ14=sQuery(id+"F12.wireOp",EDGE,"E72.1");var subQ16=sQuery(id+"F12.wireOp",EDGE,"E74.1");var subQ18=sQuery(id+"F12.wireOp",EDGE,"E74.8");Q0=qUnion([makeQuery(id+"F12.imprint","IMPRINT",FACE,{"disambiguationData":[TD([[makeQuery(id+"F12.imprint","IMPRINT",EDGE,{"derivedFrom":subQ7}),1.0]])]}),makeQuery(id+"F12.imprint","IMPRINT",FACE,{"disambiguationData":[TD([[makeQuery(id+"F12.imprint","IMPRINT",EDGE,{"derivedFrom":subQ14}),1.0]])]}),makeQuery(id+"F12.imprint","IMPRINT",FACE,{"disambiguationData":[TD([[makeQuery(id+"F12.imprint","IMPRINT",EDGE,{"derivedFrom":subQ16}),1.0]])]}),makeQuery(id+"F12.imprint","IMPRINT",FACE,{"disambiguationData":[TD([[makeQuery(id+"F12.imprint","IMPRINT",EDGE,{"derivedFrom":subQ18}),-1.0]])]})]);}
            var Q1;
            Q1=makeQuery(id+"F5.boolean.opBoolean","SPLIT",FACE,{"disambiguationData":[TD([makeQuery(id+"F5.opExtrude","SWEPT_FACE",FACE,{"disambiguationData":[OSD([sQuery(id+"F4.wireOp",EDGE,"E41")])]})])],"derivedFrom":makeQuery(id+"F3.boolean.opBoolean","COPY",FACE,{"derivedFrom":makeQuery(id+"F3.opExtrude","CAP_FACE",FACE,{"disambiguationData":[OSD([sQuery(id+"F0.wireOp",EDGE,"E25.0"),sQuery(id+"F0.wireOp",EDGE,"E25.1"),sQuery(id+"F0.wireOp",EDGE,"E25.2"),sQuery(id+"F0.wireOp",EDGE,"E25.3"),sQuery(id+"F0.wireOp",EDGE,"E25.4"),sQuery(id+"F0.wireOp",EDGE,"E25.5"),sQuery(id+"F0.wireOp",EDGE,"E25.6"),sQuery(id+"F0.wireOp",EDGE,"E25.7")])],"isStart":false})})});
            extrude(context, id + "F13", {"entities" : qUnion([Q0]), "operationType" : NewBodyOperationType.REMOVE, "endBound" : BoundingType.UP_TO_SURFACE, "endBoundEntityFace" : qUnion([Q1]), "depth" : 25 * mm});
        }
        {
            var Q0;
            Q0=makeQuery(id+"F3.boolean.opBoolean","COPY",EDGE,{"derivedFrom":makeQuery(id+"F3.opExtrude","CAP_EDGE",EDGE,{"disambiguationData":[OSD([sQuery(id+"F0.wireOp",EDGE,"E25.6")])],"isStart":false})});
            var Q1;
            Q1=makeQuery(id+"F8.boolean.opBoolean","INTERSECT",EDGE,{"derivedFrom":[makeQuery(id+"F5.opExtrude","SWEPT_FACE",FACE,{"disambiguationData":[OSD([sQuery(id+"F4.wireOp",EDGE,"E30")])]}),makeQuery(id+"F8.opExtrude","CAP_FACE",FACE,{"disambiguationData":[OSD([sQuery(id+"F7.wireOp",EDGE,"E67")])],"isStart":false})]});
            var Q2;
            Q2=makeQuery(id+"F8.boolean.opBoolean","INTERSECT",EDGE,{"disambiguationData":[OD(1.0)],"derivedFrom":[makeQuery(id+"F5.opExtrude","SWEPT_FACE",FACE,{"disambiguationData":[OSD([sQuery(id+"F4.wireOp",EDGE,"E30")])]}),makeQuery(id+"F8.opExtrude","SWEPT_FACE",FACE,{"disambiguationData":[OSD([sQuery(id+"F7.wireOp",EDGE,"E67")])]})]});
            var Q3;
            {var subQ0=sQuery(id+"F4.wireOp",EDGE,"E30");Q3=makeQuery(id+"F8.boolean.opBoolean","SPLIT",EDGE,{"disambiguationData":[TD([makeQuery(id+"F5.opExtrude","SWEPT_FACE",FACE,{"disambiguationData":[OSD([sQuery(id+"F4.wireOp",EDGE,"E35.filletArc")])]})])],"derivedFrom":makeQuery(id+"F5.opExtrude","CAP_EDGE",EDGE,{"disambiguationData":[OSD([subQ0])],"isStart":false})});}
            var Q4;
            {var subQ0=sQuery(id+"F0.wireOp",EDGE,"E25.7");var subQ1=sQuery(id+"F0.wireOp",EDGE,"E25.1");var subQ2=sQuery(id+"F0.wireOp",EDGE,"E25.6");var subQ3=sQuery(id+"F0.wireOp",EDGE,"E25.5");var subQ4=sQuery(id+"F0.wireOp",EDGE,"E25.4");var subQ5=sQuery(id+"F0.wireOp",EDGE,"E25.0");var subQ6=sQuery(id+"F0.wireOp",EDGE,"E25.2");var subQ7=sQuery(id+"F0.wireOp",EDGE,"E25.3");Q4=makeQuery(id+"F8.boolean.opBoolean","INTERSECT",EDGE,{"derivedFrom":[makeQuery(id+"F5.boolean.opBoolean","SPLIT",FACE,{"disambiguationData":[TD([makeQuery(id+"F2.opExtrude","SWEPT_FACE",FACE,{"disambiguationData":[OSD([subQ5])]})])],"derivedFrom":makeQuery(id+"F3.boolean.opBoolean","COPY",FACE,{"derivedFrom":makeQuery(id+"F3.opExtrude","CAP_FACE",FACE,{"disambiguationData":[OSD([subQ5,subQ1,subQ6,subQ7,subQ4,subQ3,subQ2,subQ0])],"isStart":false})})}),makeQuery(id+"F8.opExtrude","SWEPT_FACE",FACE,{"disambiguationData":[OSD([sQuery(id+"F7.wireOp",EDGE,"E67")])]})]});}
            var Q5;
            Q5=makeQuery(id+"F8.boolean.opBoolean","INTERSECT",EDGE,{"disambiguationData":[OD(0.0)],"derivedFrom":[makeQuery(id+"F5.opExtrude","SWEPT_FACE",FACE,{"disambiguationData":[OSD([sQuery(id+"F4.wireOp",EDGE,"E30")])]}),makeQuery(id+"F8.opExtrude","SWEPT_FACE",FACE,{"disambiguationData":[OSD([sQuery(id+"F7.wireOp",EDGE,"E67")])]})]});
            fillet(context, id + "F14", {"entities" : qUnion([Q0, Q1, Q2, Q3, Q4, Q5]), "radius" : 3 * mm, "tangentPropagation" : true, "allowEdgeOverflow" : false});
        }
        {
            var Q0;
            Q0=makeQuery(id+"F1.opExtrude","CAP_EDGE",EDGE,{"disambiguationData":[OSD([sQuery(id+"F0.wireOp",EDGE,"E1.bottom")])],"isStart":false});
            fillet(context, id + "F15", {"entities" : qUnion([Q0]), "radius" : 2 * mm, "tangentPropagation" : true, "allowEdgeOverflow" : false});
        }
        {
            var Q0;
            {var subQ0=sQuery(id+"F0.wireOp",EDGE,"E21.filletArc");var subQ1=sQuery(id+"F0.wireOp",EDGE,"E7");var subQ2=sQuery(id+"F0.wireOp",EDGE,"E6");var subQ3=sQuery(id+"F0.wireOp",EDGE,"E5");var subQ4=sQuery(id+"F0.wireOp",EDGE,"E4");var subQ5=sQuery(id+"F0.wireOp",EDGE,"E22.filletArc");var subQ6=sQuery(id+"F0.wireOp",EDGE,"E1.bottom");var subQ7=sQuery(id+"F0.wireOp",EDGE,"E1.right");var subQ8=sQuery(id+"F0.wireOp",EDGE,"E1.top");var subQ9=sQuery(id+"F0.wireOp",EDGE,"E1.left");var subQ10=sQuery(id+"F0.wireOp",EDGE,"E23.filletArc");var subQ11=sQuery(id+"F0.wireOp",EDGE,"E24.filletArc");Q0=makeQuery(id+"F2.boolean.opBoolean","SPLIT",FACE,{"disambiguationData":[TD([makeQuery(id+"F1.opExtrude","SWEPT_FACE",FACE,{"disambiguationData":[OSD([subQ6])]})])],"derivedFrom":makeQuery(id+"F1.opExtrude","CAP_FACE",FACE,{"disambiguationData":[OSD([subQ6,subQ8,subQ9,subQ7,subQ4,subQ3,subQ2,subQ1,subQ0,subQ5,subQ10,subQ11])],"isStart":true})});}
            var sketch = newSketch(context, id + "F16", { "sketchPlane" : qUnion([Q0])});
            skLineSegment(sketch, "E79", {"start": v(0, 74.25) * mm, "end": v(0, 104.25) * mm, "construction": true});
            skArc(sketch, "E80", {"start": v(15, 104.25) * mm, "mid": v(0, 119.25) * mm, "end": v(-15, 104.25) * mm});
            skLineSegment(sketch, "E81", {"start": v(15, 104.25) * mm, "end": v(15, 92.25) * mm});
            skLineSegment(sketch, "E82", {"start": v(-15, 104.25) * mm, "end": v(-15, 92.25) * mm});
            skLineSegment(sketch, "E83", {"start": v(15, 92.25) * mm, "end": v(33, 74.25) * mm});
            skLineSegment(sketch, "E84", {"start": v(-15, 92.25) * mm, "end": v(-33, 74.25) * mm});
            skCircle(sketch, "E85", {"center": v(0, 104.25) * mm, "radius": 6 * mm});
            skLineSegment(sketch, "E86", {"start": v(-74.25, 0) * mm, "end": v(74.25, 0) * mm, "construction": true});
            skLineSegment(sketch, "E87.MirrorCS", {"start": v(0, -74.25) * mm, "end": v(0, -104.25) * mm, "construction": true});
            skArc(sketch, "E88.MirrorCS", {"start": v(15, -104.25) * mm, "mid": v(0, -119.25) * mm, "end": v(-15, -104.25) * mm});
            skCircle(sketch, "E89.MirrorC", {"center": v(0, -104.25) * mm, "radius": 6 * mm});
            skLineSegment(sketch, "E90.MirrorCS", {"start": v(-15, -92.25) * mm, "end": v(-33, -74.25) * mm});
            skLineSegment(sketch, "E91.MirrorCS", {"start": v(15, -104.25) * mm, "end": v(15, -92.25) * mm});
            skLineSegment(sketch, "E92.MirrorCS", {"start": v(-15, -104.25) * mm, "end": v(-15, -92.25) * mm});
            skLineSegment(sketch, "E93.MirrorCS", {"start": v(15, -92.25) * mm, "end": v(33, -74.25) * mm});
            skSolve(sketch);
        }
        {
            var Q0;
            Q0=makeQuery(id+"F16.imprint","IMPRINT",FACE,{"disambiguationData":[TD([[makeQuery(id+"F16.imprint","IMPRINT",EDGE,{"derivedFrom":sQuery(id+"F16.wireOp",EDGE,"E80")}),1.0]])]});
            var Q1;
            Q1=makeQuery(id+"F16.imprint","IMPRINT",FACE,{"disambiguationData":[TD([[makeQuery(id+"F16.imprint","IMPRINT",EDGE,{"derivedFrom":makeQuery(id+"F1.opExtrude","CAP_EDGE",EDGE,{"disambiguationData":[OSD([sQuery(id+"F0.wireOp",EDGE,"E1.left")])],"isStart":true})}),-1.0]])]});
            var Q2;
            Q2=makeQuery(id+"F16.imprint","IMPRINT",FACE,{"disambiguationData":[TD([[makeQuery(id+"F16.imprint","IMPRINT",EDGE,{"derivedFrom":sQuery(id+"F16.wireOp",EDGE,"E88.MirrorCS")}),-1.0]])]});
            var Q3;
            Q3=makeQuery(id+"F2.opExtrude","CAP_FACE",FACE,{"disambiguationData":[OSD([sQuery(id+"F0.wireOp",EDGE,"E12"),sQuery(id+"F0.wireOp",EDGE,"E13"),sQuery(id+"F0.wireOp",EDGE,"E14"),sQuery(id+"F0.wireOp",EDGE,"E15"),sQuery(id+"F0.wireOp",EDGE,"E17.filletArc"),sQuery(id+"F0.wireOp",EDGE,"E18.filletArc"),sQuery(id+"F0.wireOp",EDGE,"E19.filletArc"),sQuery(id+"F0.wireOp",EDGE,"E20.filletArc"),sQuery(id+"F0.wireOp",EDGE,"E25.0"),sQuery(id+"F0.wireOp",EDGE,"E25.1"),sQuery(id+"F0.wireOp",EDGE,"E25.2"),sQuery(id+"F0.wireOp",EDGE,"E25.3"),sQuery(id+"F0.wireOp",EDGE,"E25.4"),sQuery(id+"F0.wireOp",EDGE,"E25.5"),sQuery(id+"F0.wireOp",EDGE,"E25.6"),sQuery(id+"F0.wireOp",EDGE,"E25.7")])],"isStart":false});
            extrude(context, id + "F17", {"entities" : qUnion([Q0, Q1, Q2]), "endBound" : BoundingType.UP_TO_SURFACE, "endBoundEntityFace" : qUnion([Q3]), "depth" : 25 * mm});
        }
    });
